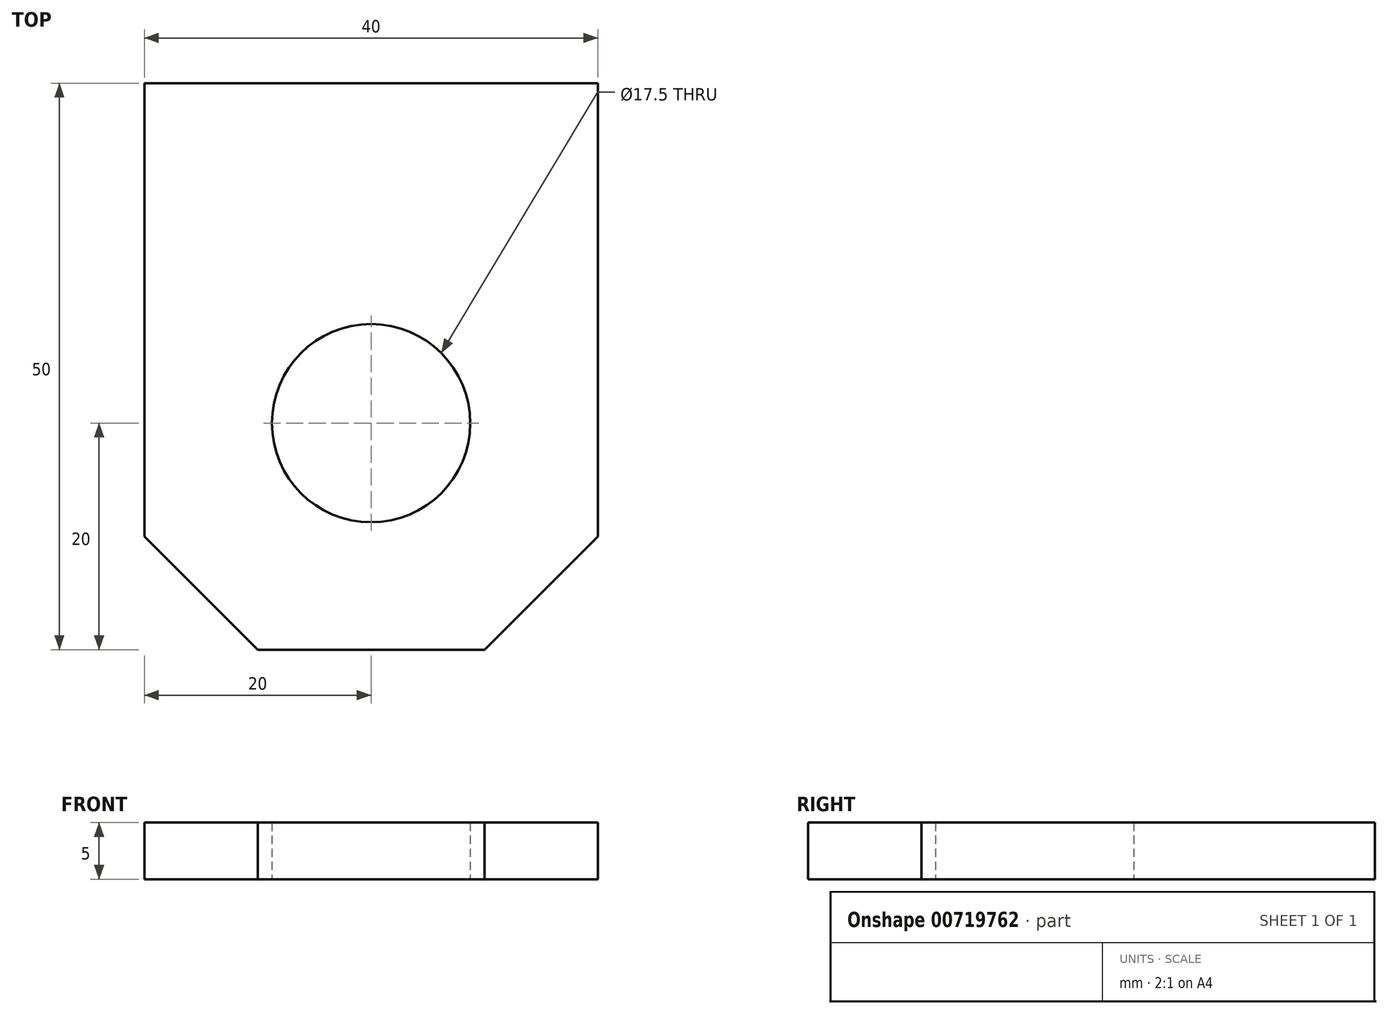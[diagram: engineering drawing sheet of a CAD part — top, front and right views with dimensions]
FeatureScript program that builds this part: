
annotation { "Feature Type Name" : "Feature", "Feature Type Description" : "" }
export const myFeature = defineFeature(function(context is Context, id is Id, definition is map)
    precondition{}
    {
        {
            var Q0;
            Q0=qCreatedBy(makeId("Top.planeOp"),FACE);
            var sketch = newSketch(context, id + "F0", { "sketchPlane" : qUnion([Q0])});
            skLineSegment(sketch, "E0", {"start": v(0, 0) * mm, "end": v(20, 0) * mm});
            skLineSegment(sketch, "E1", {"start": v(0, 0) * mm, "end": v(-20, 0) * mm});
            skLineSegment(sketch, "E2", {"start": v(-20, 0) * mm, "end": v(-20, -50) * mm});
            skLineSegment(sketch, "E3", {"start": v(20, 0) * mm, "end": v(20, -50) * mm});
            skLineSegment(sketch, "E4", {"start": v(-20, -50) * mm, "end": v(20, -50) * mm});
            skCircle(sketch, "E5", {"center": v(0, -30) * mm, "radius": 8.75 * mm});
            skSolve(sketch);
        }
        {
            var Q0;
            Q0=makeQuery(id+"F0.imprint","IMPRINT",FACE,{"disambiguationData":[TD([[makeQuery(id+"F0.imprint","IMPRINT",EDGE,{"derivedFrom":sQuery(id+"F0.wireOp",EDGE,"E0")}),-1.0]])]});
            extrude(context, id + "F1", {"entities" : qUnion([Q0]), "depth" : 5 * mm, "offsetDistance" : 25 * mm});
        }
        {
            var Q0;
            Q0=makeQuery(id+"F1.opExtrude","SWEPT_EDGE",EDGE,{"disambiguationData":[OSD([sQuery(id+"F0.wireOp",EDGE,"E2"),sQuery(id+"F0.wireOp",EDGE,"E4")])]});
            var Q1;
            Q1=makeQuery(id+"F1.opExtrude","SWEPT_EDGE",EDGE,{"disambiguationData":[OSD([sQuery(id+"F0.wireOp",EDGE,"E3"),sQuery(id+"F0.wireOp",EDGE,"E4")])]});
            chamfer(context, id + "F2", {"entities" : qUnion([Q0, Q1]), "width" : 10 * mm, "tangentPropagation" : true});
        }
    });
